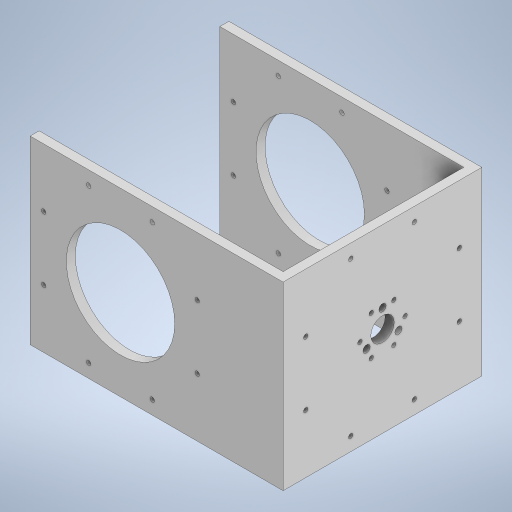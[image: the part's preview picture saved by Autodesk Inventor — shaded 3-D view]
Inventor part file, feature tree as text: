
AUTODESK INVENTOR PART (.ipt)
format: ipt  version: 2024.3 (Build 283343000, 343)  size: 335,872 bytes
history: native  units: mm
features: sketch x12, extrude x8, hole x4, other x1
ambient origin geometry x8: Origin, YZ Plane, XZ Plane, XY Plane, X Axis, Y Axis, Z Axis, Center Point
bodies: Body1 (feature_tree)
feature tree (25):
  other  "ソリッド1"
  extrude  "押し出し1"  Depth=97.0mm
  hole  "穴1"  [1 undecoded]
  extrude  "押し出し2"  Depth=50.0mm
  extrude  "押し出し3"  Depth=50.0mm
  extrude  "押し出し4"  Depth=50.0mm
  hole  "穴2"  [1 undecoded]
  hole  "穴3"  [1 undecoded]
  extrude  "押し出し5"  TaperAngle=22.5deg  [1 undecoded]
  extrude  "押し出し6"  Depth=80.0mm TaperAngle=360.0deg
  extrude  "押し出し7"  Depth=60.0mm
  hole  "穴4"  [1 undecoded]
  extrude  "押し出し8"  Depth=40.0mm TaperAngle=0.0deg
  sketch  "スケッチ1"
  sketch  "スケッチ2"
  sketch  "スケッチ3"
  sketch  "スケッチ4"
  sketch  "スケッチ5"
  sketch  "スケッチ6"
  sketch  "スケッチ7"
  sketch  "スケッチ8"
  sketch  "スケッチ9"
  sketch  "スケッチ10"
  sketch  "スケッチ11"
  sketch  "スケッチ12"
note: 5 required parameter values undecoded (feature->parameter linkage not recoverable at this tier; creation-order binding heuristic only, values carry confidence <= 0.55)
